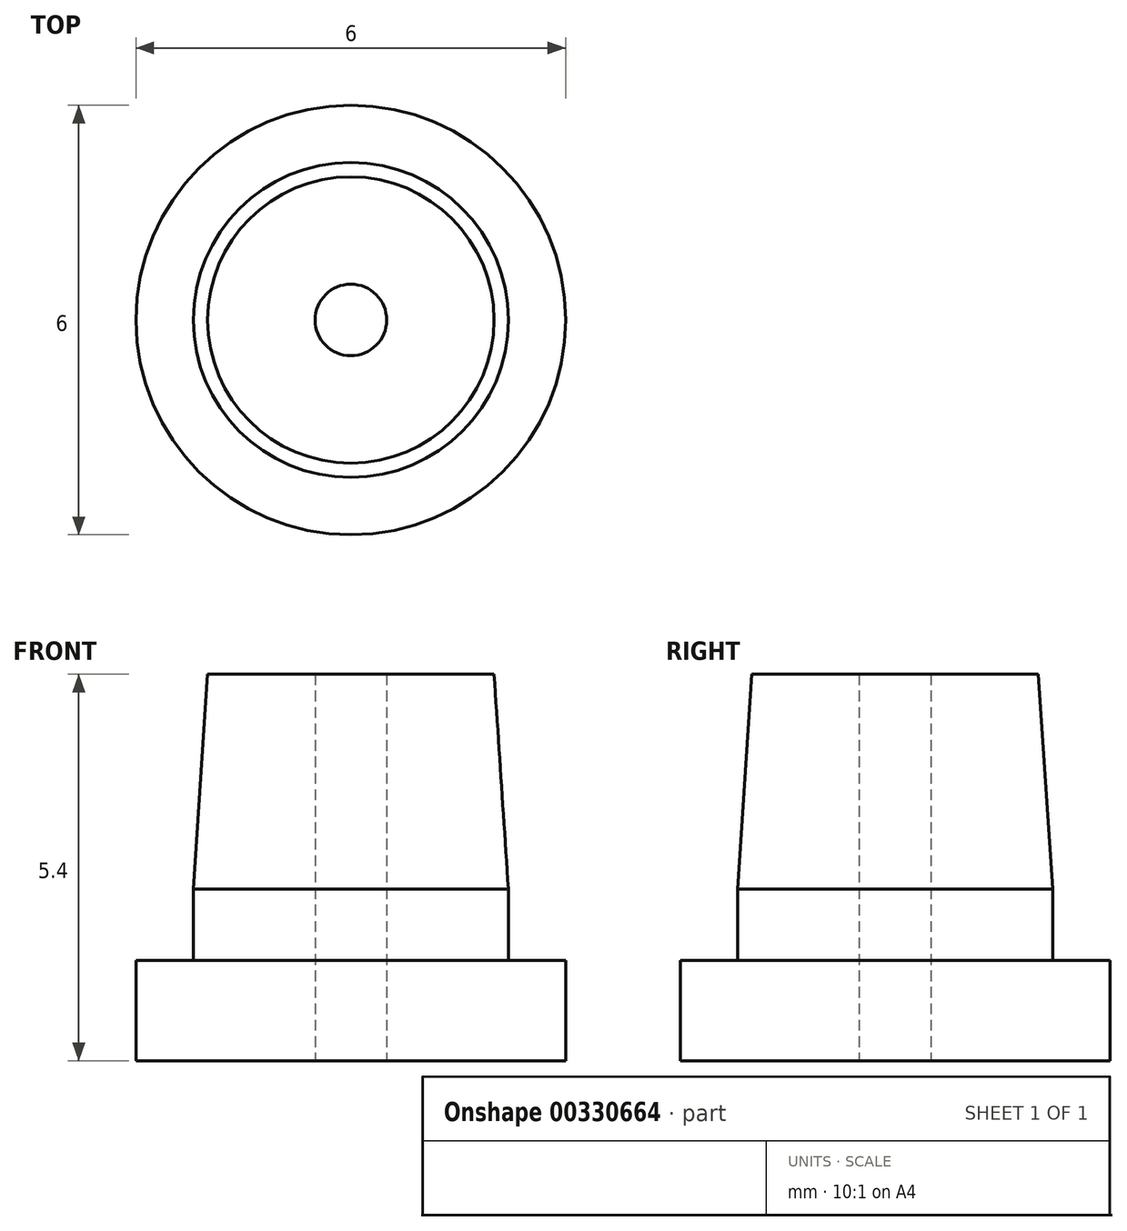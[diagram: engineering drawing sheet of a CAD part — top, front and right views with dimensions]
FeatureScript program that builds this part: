
annotation { "Feature Type Name" : "Feature", "Feature Type Description" : "" }
export const myFeature = defineFeature(function(context is Context, id is Id, definition is map)
    precondition{}
    {
        {
            var Q0;
            Q0=qCreatedBy(makeId("Top.planeOp"),FACE);
            var sketch = newSketch(context, id + "F0", { "sketchPlane" : qUnion([Q0])});
            skCircle(sketch, "E0", {"center": v(0, 0) * mm, "radius": 3 * mm});
            skCircle(sketch, "E1", {"center": v(0, 0) * mm, "radius": 0.5 * mm});
            skSolve(sketch);
        }
        {
            var Q0;
            Q0=makeQuery(id+"F0.imprint","IMPRINT",FACE,{"disambiguationData":[TD([[makeQuery(id+"F0.imprint","IMPRINT",EDGE,{"derivedFrom":sQuery(id+"F0.wireOp",EDGE,"E0")}),1.0]])]});
            extrude(context, id + "F1", {"entities" : qUnion([Q0]), "depth" : 1.4 * mm});
        }
        {
            var Q0;
            Q0=makeQuery(id+"F1.opExtrude","CAP_FACE",FACE,{"disambiguationData":[OSD([sQuery(id+"F0.wireOp",EDGE,"E0"),sQuery(id+"F0.wireOp",EDGE,"E1")])],"isStart":false});
            var sketch = newSketch(context, id + "F2", { "sketchPlane" : qUnion([Q0])});
            skCircle(sketch, "E2.0.0", {"center": v(0, 0) * mm, "radius": 3 * mm});
            skCircle(sketch, "E3", {"center": v(0, 0) * mm, "radius": 0.5 * mm});
            skCircle(sketch, "E4", {"center": v(0, 0) * mm, "radius": 2.2 * mm});
            skSolve(sketch);
        }
        {
            var Q0;
            Q0=makeQuery(id+"F2.imprint","IMPRINT",FACE,{"disambiguationData":[TD([[makeQuery(id+"F2.imprint","IMPRINT",EDGE,{"derivedFrom":sQuery(id+"F2.wireOp",EDGE,"E3")}),-1.0]])]});
            extrude(context, id + "F3", {"entities" : qUnion([Q0]), "operationType" : NewBodyOperationType.ADD, "depth" : 4 * mm});
        }
        {
            var Q0;
            Q0=makeQuery(id+"F3.opExtrude","CAP_EDGE",EDGE,{"disambiguationData":[OSD([sQuery(id+"F2.wireOp",EDGE,"E4")])],"isStart":false});
            chamfer(context, id + "F4", {"entities" : qUnion([Q0]), "chamferType" : ChamferType.TWO_OFFSETS, "width1" : 0.2 * mm, "oppositeDirection" : false, "width2" : 3 * mm, "tangentPropagation" : true});
        }
    });
